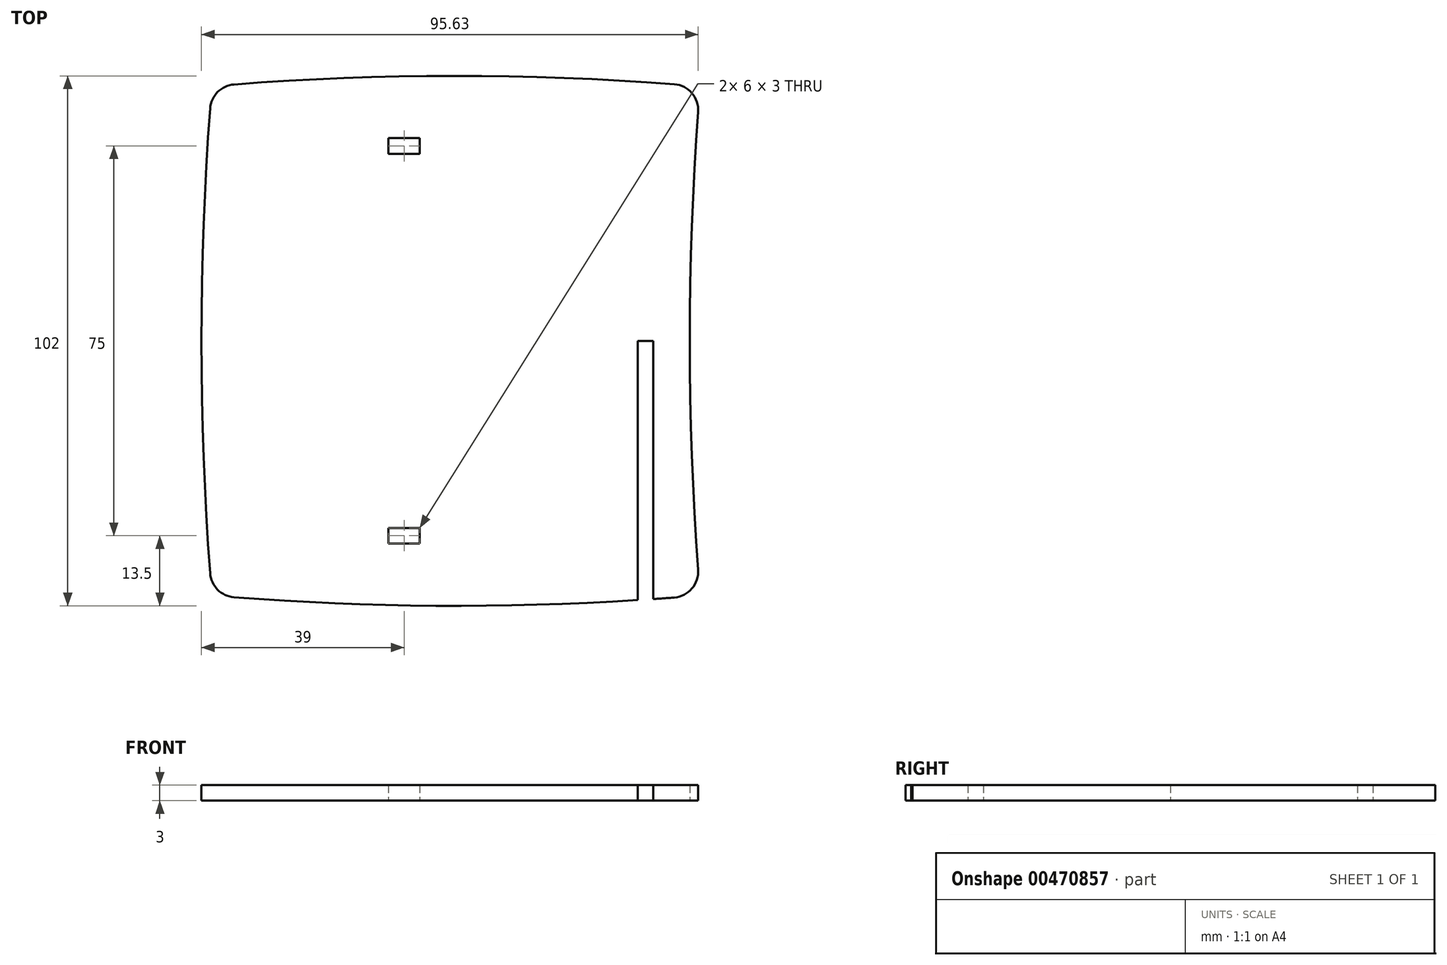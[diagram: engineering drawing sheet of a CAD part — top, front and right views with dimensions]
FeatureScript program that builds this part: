
annotation { "Feature Type Name" : "Feature", "Feature Type Description" : "" }
export const myFeature = defineFeature(function(context is Context, id is Id, definition is map)
    precondition{}
    {
        {
            assignVariable(context, id + "F0", {"name" : "WoodWidth", "anyValue" : 3});
        }
        {
            var Q0;
            Q0=qCreatedBy(makeId("Top.planeOp"),FACE);
            var sketch = newSketch(context, id + "F1", { "sketchPlane" : qUnion([Q0])});
            skPoint(sketch, "E0.middle", {"position": v(0, 0) * mm});
            skLineSegment(sketch, "E1.bottom", {"start": v(45.5, -49) * mm, "end": v(-45.5, -49) * mm});
            skLineSegment(sketch, "E1.top", {"start": v(45.5, 49) * mm, "end": v(-45.5, 49) * mm});
            skLineSegment(sketch, "E1.left", {"start": v(45.5, -49) * mm, "end": v(45.5, 49) * mm});
            skLineSegment(sketch, "E1.right", {"start": v(-45.5, -49) * mm, "end": v(-45.5, 49) * mm});
            skLineSegment(sketch, "E2.bottom", {"start": v(39.5, -49) * mm, "end": v(36.5, -49) * mm});
            skLineSegment(sketch, "E2.top", {"start": v(39.5, 0) * mm, "end": v(36.5, 0) * mm});
            skLineSegment(sketch, "E2.left", {"start": v(39.5, -49) * mm, "end": v(39.5, 0) * mm});
            skLineSegment(sketch, "E2.right", {"start": v(36.5, -49) * mm, "end": v(36.5, 0) * mm});
            skLineSegment(sketch, "E3.bottom", {"start": v(-11.5, -39) * mm, "end": v(-5.5, -39) * mm});
            skLineSegment(sketch, "E3.top", {"start": v(-11.5, -36) * mm, "end": v(-5.5, -36) * mm});
            skLineSegment(sketch, "E3.left", {"start": v(-11.5, -39) * mm, "end": v(-11.5, -36) * mm});
            skLineSegment(sketch, "E3.right", {"start": v(-5.5, -39) * mm, "end": v(-5.5, -36) * mm});
            skLineSegment(sketch, "E4.MirrorCS", {"start": v(-11.5, 36) * mm, "end": v(-5.5, 36) * mm});
            skLineSegment(sketch, "E5.MirrorCS", {"start": v(-11.5, 39) * mm, "end": v(-11.5, 36) * mm});
            skLineSegment(sketch, "E6.MirrorCS", {"start": v(-11.5, 39) * mm, "end": v(-5.5, 39) * mm});
            skLineSegment(sketch, "E7.MirrorCS", {"start": v(-5.5, 39) * mm, "end": v(-5.5, 36) * mm});
            skLineSegment(sketch, "E8.bottom", {"start": v(45.5, 49) * mm, "end": v(45.5, 49) * mm});
            skLineSegment(sketch, "E8.top", {"start": v(45.5, -49) * mm, "end": v(45.5, -49) * mm});
            skLineSegment(sketch, "E8.left", {"start": v(45.5, 49) * mm, "end": v(45.5, -49) * mm});
            skLineSegment(sketch, "E8.right", {"start": v(45.5, 49) * mm, "end": v(45.5, -49) * mm});
            skLineSegment(sketch, "E9.bottom", {"start": v(45.5, 49) * mm, "end": v(48.5, 49) * mm});
            skLineSegment(sketch, "E9.top", {"start": v(45.5, -49) * mm, "end": v(48.5, -49) * mm});
            skLineSegment(sketch, "E9.right", {"start": v(48.5, 49) * mm, "end": v(48.5, -49) * mm});
            skArc(sketch, "E10", {"start": v(48.5, 49) * mm, "mid": v(46.5, 0) * mm, "end": v(48.5, -49) * mm});
            skArc(sketch, "E11", {"start": v(-45.5, 49) * mm, "mid": v(-47.5, 0) * mm, "end": v(-45.5, -49) * mm});
            skArc(sketch, "E12", {"start": v(48.5, 49) * mm, "mid": v(1.5, 51) * mm, "end": v(-45.5, 49) * mm});
            skArc(sketch, "E13", {"start": v(-45.5, -49) * mm, "mid": v(1.5, -51) * mm, "end": v(48.5, -49) * mm});
            skLineSegment(sketch, "E14", {"start": v(36.5, -49) * mm, "end": v(36.5, -49.9) * mm});
            skLineSegment(sketch, "E15", {"start": v(36.5, -49.9) * mm, "end": v(39.5, -49.9) * mm});
            skLineSegment(sketch, "E16", {"start": v(39.5, -49) * mm, "end": v(39.5, -49.9) * mm});
            skSolve(sketch);
        }
        {
            var Q0;
            Q0=makeQuery(id+"F1.imprint","IMPRINT",FACE,{"disambiguationData":[TD([[makeQuery(id+"F1.imprint","IMPRINT",EDGE,{"derivedFrom":sQuery(id+"F1.wireOp",EDGE,"E1.top")}),1.0]])]});
            var Q1;
            Q1=makeQuery(id+"F1.imprint","IMPRINT",FACE,{"disambiguationData":[TD([[makeQuery(id+"F1.imprint","IMPRINT",EDGE,{"derivedFrom":sQuery(id+"F1.wireOp",EDGE,"E9.bottom")}),-1.0]])]});
            var Q2;
            {var subQ3=sQuery(id+"F1.wireOp",EDGE,"E14");Q2=makeQuery(id+"F1.imprint","IMPRINT",FACE,{"disambiguationData":[TD([[makeQuery(id+"F1.imprint","IMPRINT",EDGE,{"derivedFrom":subQ3}),-1.0]])]});}
            var Q3;
            {var subQ0=sQuery(id+"F1.wireOp",EDGE,"E9.top");Q3=makeQuery(id+"F1.imprint","IMPRINT",FACE,{"disambiguationData":[TD([[makeQuery(id+"F1.imprint","IMPRINT",EDGE,{"derivedFrom":subQ0}),-1.0]])]});}
            var Q4;
            Q4=makeQuery(id+"F1.imprint","IMPRINT",FACE,{"disambiguationData":[TD([[makeQuery(id+"F1.imprint","IMPRINT",EDGE,{"derivedFrom":sQuery(id+"F1.wireOp",EDGE,"E1.top")}),-1.0]])]});
            var Q5;
            Q5=makeQuery(id+"F1.imprint","IMPRINT",FACE,{"disambiguationData":[TD([[makeQuery(id+"F1.imprint","IMPRINT",EDGE,{"derivedFrom":sQuery(id+"F1.wireOp",EDGE,"E1.right")}),1.0]])]});
            extrude(context, id + "F2", {"entities" : qUnion([Q0, Q1, Q2, Q3, Q4, Q5]), "depth" : (getVariable(context, 'WoodWidth')) * mm});
        }
        {
            var Q0;
            Q0=makeQuery(id+"F2.opExtrude","SWEPT_EDGE",EDGE,{"disambiguationData":[OSD([sQuery(id+"F1.wireOp",EDGE,"E1.bottom"),sQuery(id+"F1.wireOp",EDGE,"E1.right"),sQuery(id+"F1.wireOp",EDGE,"E11"),sQuery(id+"F1.wireOp",EDGE,"E13")])]});
            var Q1;
            Q1=makeQuery(id+"F2.opExtrude","SWEPT_EDGE",EDGE,{"disambiguationData":[OSD([sQuery(id+"F1.wireOp",EDGE,"E1.top"),sQuery(id+"F1.wireOp",EDGE,"E1.right"),sQuery(id+"F1.wireOp",EDGE,"E11"),sQuery(id+"F1.wireOp",EDGE,"E12")])]});
            var Q2;
            Q2=makeQuery(id+"F2.opExtrude","SWEPT_EDGE",EDGE,{"disambiguationData":[OSD([sQuery(id+"F1.wireOp",EDGE,"E1.bottom"),sQuery(id+"F1.wireOp",EDGE,"E1.right"),sQuery(id+"F1.wireOp",EDGE,"E11"),sQuery(id+"F1.wireOp",EDGE,"E13")])]});
            var Q3;
            Q3=makeQuery(id+"F2.opExtrude","SWEPT_EDGE",EDGE,{"disambiguationData":[OSD([sQuery(id+"F1.wireOp",EDGE,"E1.top"),sQuery(id+"F1.wireOp",EDGE,"E1.right"),sQuery(id+"F1.wireOp",EDGE,"E11"),sQuery(id+"F1.wireOp",EDGE,"E12")])]});
            var Q4;
            Q4=makeQuery(id+"F2.opExtrude","SWEPT_EDGE",EDGE,{"disambiguationData":[OSD([sQuery(id+"F1.wireOp",EDGE,"E9.top"),sQuery(id+"F1.wireOp",EDGE,"E9.right"),sQuery(id+"F1.wireOp",EDGE,"E10"),sQuery(id+"F1.wireOp",EDGE,"E13")])]});
            var Q5;
            Q5=makeQuery(id+"F2.opExtrude","SWEPT_EDGE",EDGE,{"disambiguationData":[OSD([sQuery(id+"F1.wireOp",EDGE,"E9.bottom"),sQuery(id+"F1.wireOp",EDGE,"E9.right"),sQuery(id+"F1.wireOp",EDGE,"E10"),sQuery(id+"F1.wireOp",EDGE,"E12")])]});
            fillet(context, id + "F3", {"entities" : qUnion([Q0, Q1, Q2, Q3, Q4, Q5]), "radius" : 5 * mm, "tangentPropagation" : true, "allowEdgeOverflow" : false});
        }
    });
